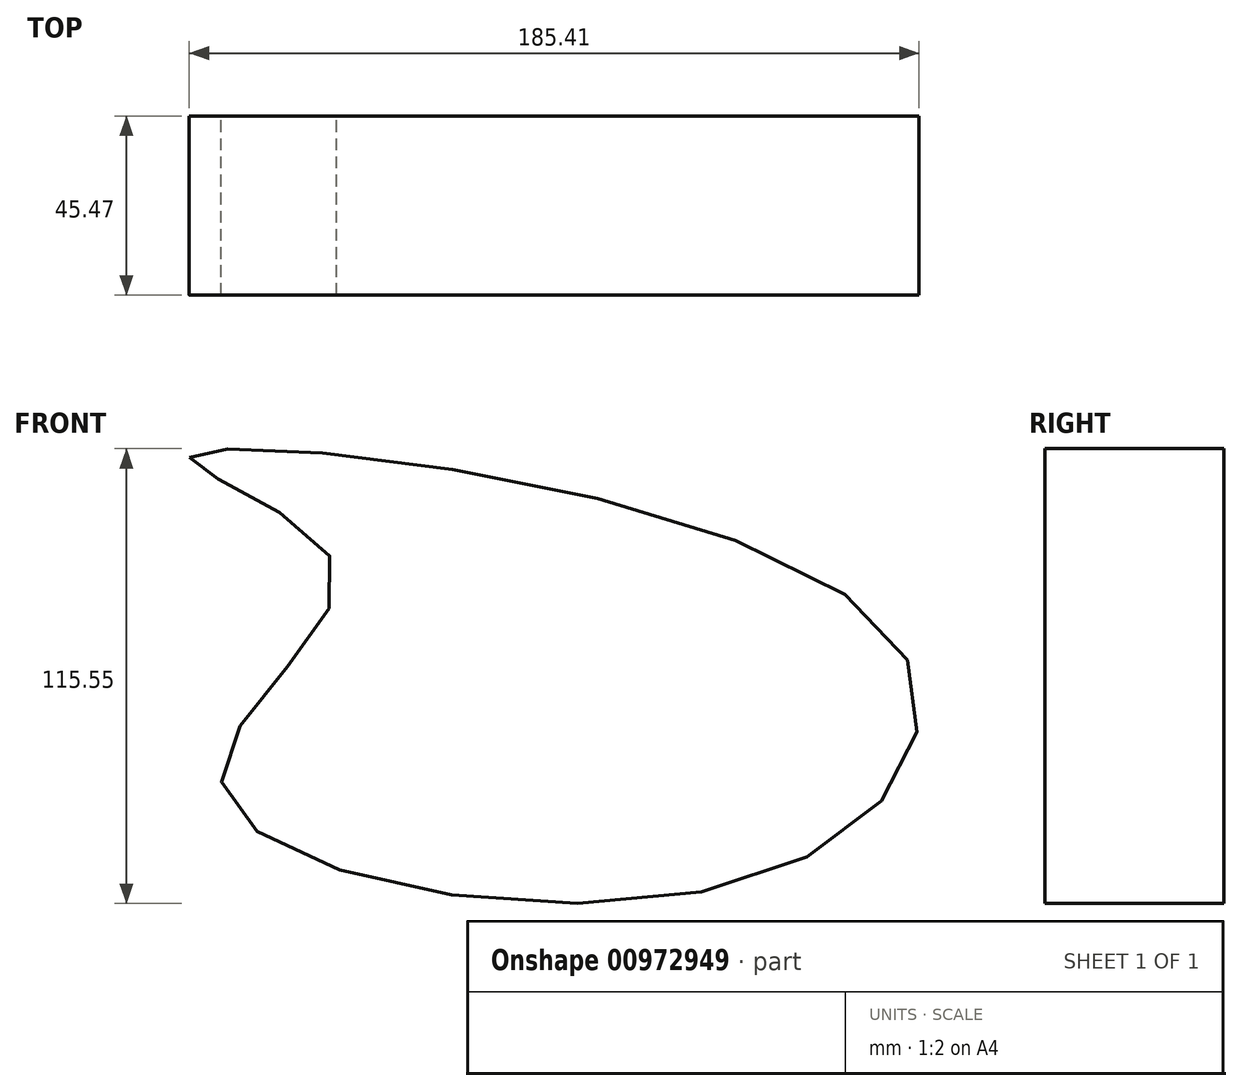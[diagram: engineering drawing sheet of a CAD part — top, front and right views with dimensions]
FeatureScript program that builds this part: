
annotation { "Feature Type Name" : "Feature", "Feature Type Description" : "" }
export const myFeature = defineFeature(function(context is Context, id is Id, definition is map)
    precondition{}
    {
        {
            var Q0;
            Q0=qCreatedBy(makeId("Front.planeOp"),FACE);
            var sketch = newSketch(context, id + "F0", { "sketchPlane" : qUnion([Q0])});
            skFitSpline(sketch, "E0", {"points": [v(-114.2, 53.19) * mm, v(-77.2, 25.13) * mm, v(-106.1, -28.9) * mm, v(34.4, -51.94) * mm, v(59.85, 12.65) * mm, v(-114.2, 53.19) * mm]});
            skSolve(sketch);
        }
        {
            var Q0;
            Q0=makeQuery(id+"F0.imprint","IMPRINT",FACE,{"disambiguationData":[TD([[makeQuery(id+"F0.imprint","IMPRINT",EDGE,{"derivedFrom":sQuery(id+"F0.wireOp",EDGE,"E0")}),1.0]])]});
            extrude(context, id + "F1", {"entities" : qUnion([Q0]), "depth" : 45.47 * mm, "offsetDistance" : 25.4 * mm});
        }
    });
